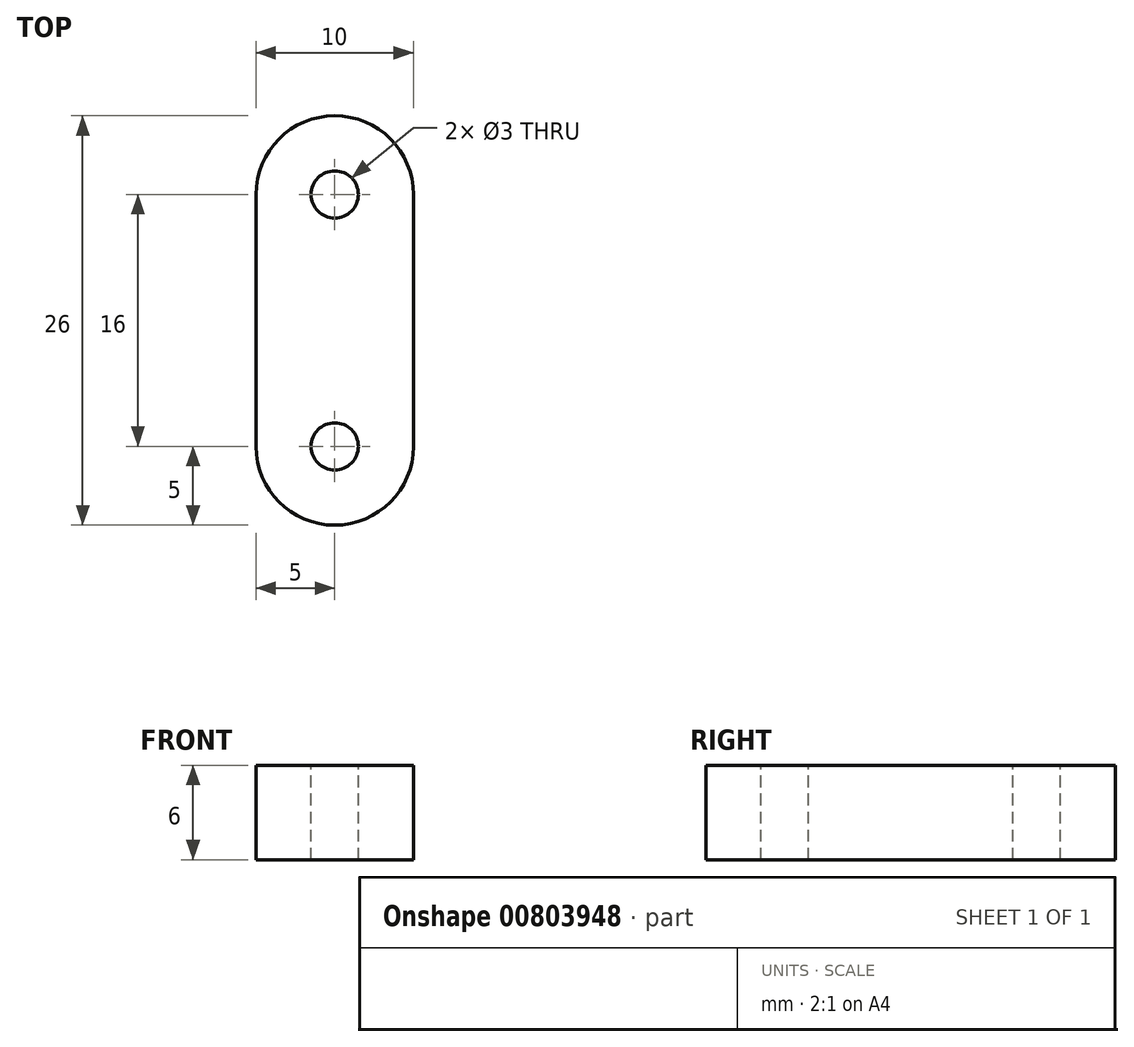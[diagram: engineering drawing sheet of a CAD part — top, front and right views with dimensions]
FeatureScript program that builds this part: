
annotation { "Feature Type Name" : "Feature", "Feature Type Description" : "" }
export const myFeature = defineFeature(function(context is Context, id is Id, definition is map)
    precondition{}
    {
        {
            var Q0;
            Q0=qCreatedBy(makeId("Top.planeOp"),FACE);
            var sketch = newSketch(context, id + "F0", { "sketchPlane" : qUnion([Q0])});
            skLineSegment(sketch, "E0.bottom", {"start": v(-5, 8) * mm, "end": v(5, 8) * mm});
            skLineSegment(sketch, "E0.top", {"start": v(-5, -8) * mm, "end": v(5, -8) * mm});
            skLineSegment(sketch, "E0.left", {"start": v(-5, 8) * mm, "end": v(-5, -8) * mm});
            skLineSegment(sketch, "E0.right", {"start": v(5, 8) * mm, "end": v(5, -8) * mm});
            skPoint(sketch, "E0.middle", {"position": v(0, 0) * mm});
            skArc(sketch, "E1", {"start": v(-5, 8) * mm, "mid": v(0, 13) * mm, "end": v(5, 8) * mm});
            skArc(sketch, "E2", {"start": v(5, -8) * mm, "mid": v(0, -13) * mm, "end": v(-5, -8) * mm});
            skSolve(sketch);
        }
        {
            var Q0;
            Q0=makeQuery(id+"F0.imprint","IMPRINT",FACE,{"disambiguationData":[TD([[makeQuery(id+"F0.imprint","IMPRINT",EDGE,{"derivedFrom":sQuery(id+"F0.wireOp",EDGE,"E0.bottom")}),1.0]])]});
            var Q1;
            Q1=makeQuery(id+"F0.imprint","IMPRINT",FACE,{"disambiguationData":[TD([[makeQuery(id+"F0.imprint","IMPRINT",EDGE,{"derivedFrom":sQuery(id+"F0.wireOp",EDGE,"E0.bottom")}),-1.0]])]});
            var Q2;
            Q2=makeQuery(id+"F0.imprint","IMPRINT",FACE,{"disambiguationData":[TD([[makeQuery(id+"F0.imprint","IMPRINT",EDGE,{"derivedFrom":sQuery(id+"F0.wireOp",EDGE,"E0.top")}),-1.0]])]});
            extrude(context, id + "F1", {"entities" : qUnion([Q0, Q1, Q2]), "depth" : 6 * mm, "offsetDistance" : 25 * mm});
        }
        {
            var Q0;
            Q0=sQuery(id+"F0.wireOp",VERTEX,"E1.center");
            var Q1;
            Q1=sQuery(id+"F0.wireOp",VERTEX,"E2.center");
            var Q2;
            Q2=makeQuery(id+"F1.opExtrude","SWEPT_BODY",BODY,{"disambiguationData":[OSD([sQuery(id+"F0.wireOp",EDGE,"E0.left"),sQuery(id+"F0.wireOp",EDGE,"E0.right"),sQuery(id+"F0.wireOp",EDGE,"E1"),sQuery(id+"F0.wireOp",EDGE,"E2")])]});
            hole(context, id + "F2", {"style" : HoleStyle.SIMPLE, "endStyle" : HoleEndStyle.THROUGH, "oppositeDirection" : true, "holeDiameter" : 3 * mm, "majorDiameter" : 5 * mm, "isTappedThrough" : true, "tappedDepth" : 12 * mm, "tapClearance" : 3, "locations" : qUnion([Q0, Q1]), "scope" : qUnion([Q2])});
        }
    });
